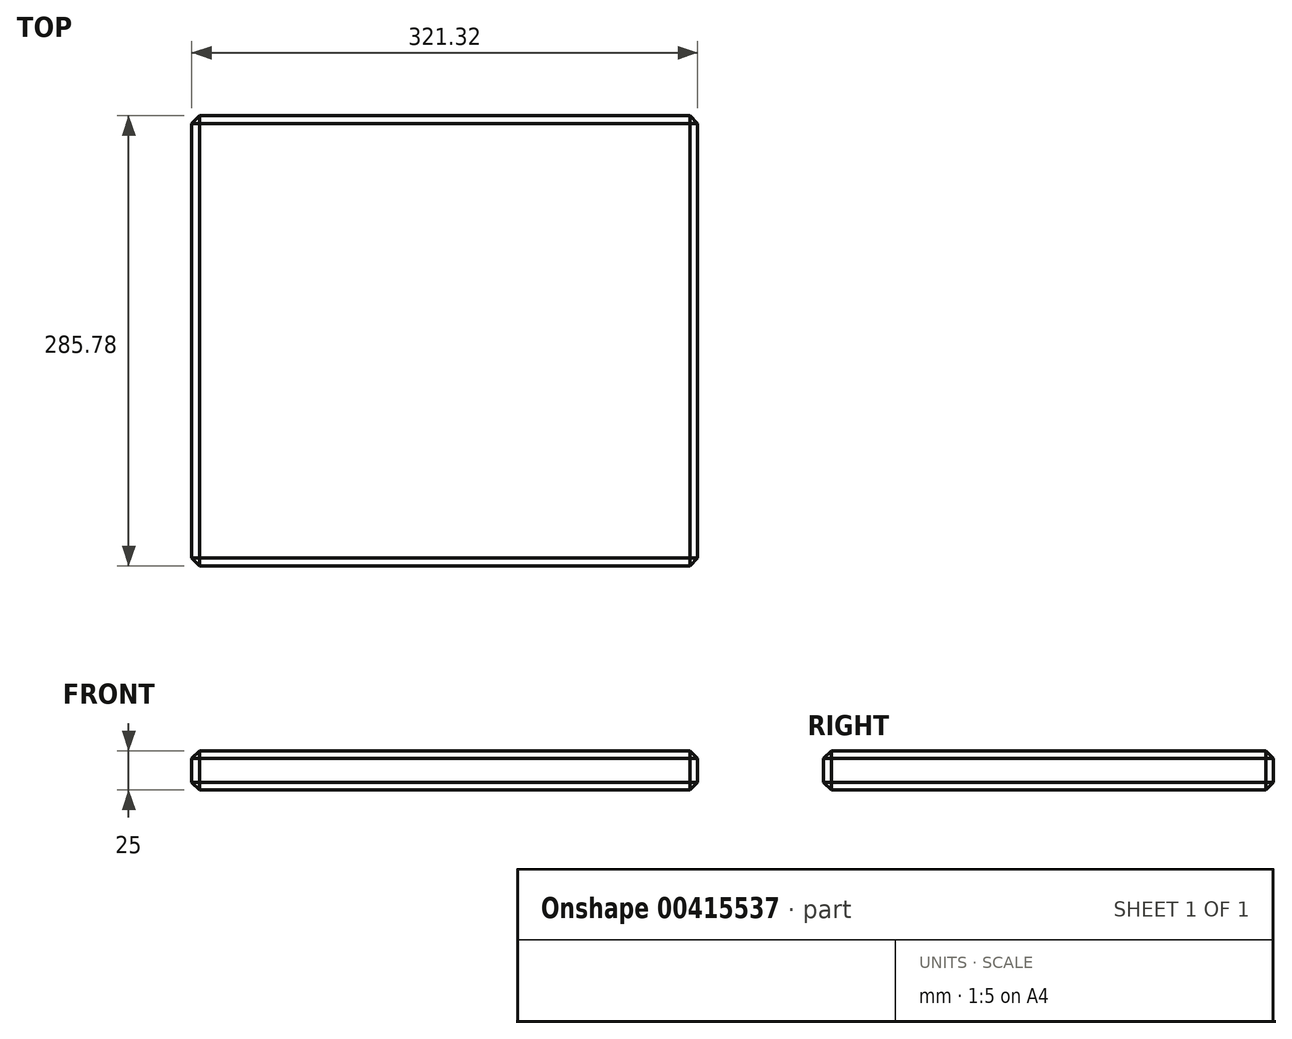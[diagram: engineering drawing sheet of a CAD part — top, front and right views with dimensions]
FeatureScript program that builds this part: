
annotation { "Feature Type Name" : "Feature", "Feature Type Description" : "" }
export const myFeature = defineFeature(function(context is Context, id is Id, definition is map)
    precondition{}
    {
        {
            var Q0;
            Q0=qCreatedBy(makeId("Top.planeOp"),FACE);
            var sketch = newSketch(context, id + "F0", { "sketchPlane" : qUnion([Q0])});
            skLineSegment(sketch, "E0.bottom", {"start": v(160.66, 142.89) * mm, "end": v(-160.66, 142.89) * mm});
            skLineSegment(sketch, "E0.top", {"start": v(160.66, -142.89) * mm, "end": v(-160.66, -142.89) * mm});
            skLineSegment(sketch, "E0.left", {"start": v(160.66, 142.89) * mm, "end": v(160.66, -142.89) * mm});
            skLineSegment(sketch, "E0.right", {"start": v(-160.66, 142.89) * mm, "end": v(-160.66, -142.89) * mm});
            skPoint(sketch, "E0.middle", {"position": v(0, 0) * mm});
            skSolve(sketch);
        }
        {
            var Q0;
            Q0=makeQuery(id+"F0.imprint","IMPRINT",FACE,{"disambiguationData":[TD([[makeQuery(id+"F0.imprint","IMPRINT",EDGE,{"derivedFrom":sQuery(id+"F0.wireOp",EDGE,"E0.bottom")}),1.0]])]});
            extrude(context, id + "F1", {"entities" : qUnion([Q0]), "depth" : 25 * mm});
        }
        {
            var Q0;
            Q0=makeQuery(id+"F1.opExtrude","SWEPT_EDGE",EDGE,{"disambiguationData":[OSD([sQuery(id+"F0.wireOp",EDGE,"E0.bottom"),sQuery(id+"F0.wireOp",EDGE,"E0.left")])]});
            var Q1;
            Q1=makeQuery(id+"F1.opExtrude","SWEPT_EDGE",EDGE,{"disambiguationData":[OSD([sQuery(id+"F0.wireOp",EDGE,"E0.top"),sQuery(id+"F0.wireOp",EDGE,"E0.left")])]});
            var Q2;
            Q2=makeQuery(id+"F1.opExtrude","CAP_EDGE",EDGE,{"disambiguationData":[OSD([sQuery(id+"F0.wireOp",EDGE,"E0.left")])],"isStart":true});
            var Q3;
            Q3=makeQuery(id+"F1.opExtrude","CAP_EDGE",EDGE,{"disambiguationData":[OSD([sQuery(id+"F0.wireOp",EDGE,"E0.top")])],"isStart":true});
            var Q4;
            Q4=makeQuery(id+"F1.opExtrude","SWEPT_FACE",FACE,{"disambiguationData":[OSD([sQuery(id+"F0.wireOp",EDGE,"E0.bottom")])]});
            var Q5;
            Q5=makeQuery(id+"F1.opExtrude","SWEPT_FACE",FACE,{"disambiguationData":[OSD([sQuery(id+"F0.wireOp",EDGE,"E0.left")])]});
            var Q6;
            Q6=makeQuery(id+"F1.opExtrude","CAP_FACE",FACE,{"disambiguationData":[OSD([sQuery(id+"F0.wireOp",EDGE,"E0.bottom"),sQuery(id+"F0.wireOp",EDGE,"E0.top"),sQuery(id+"F0.wireOp",EDGE,"E0.left"),sQuery(id+"F0.wireOp",EDGE,"E0.right")])],"isStart":false});
            var Q7;
            Q7=makeQuery(id+"F1.opExtrude","SWEPT_FACE",FACE,{"disambiguationData":[OSD([sQuery(id+"F0.wireOp",EDGE,"E0.right")])]});
            chamfer(context, id + "F2", {"entities" : qUnion([Q0, Q1, Q2, Q3, Q4, Q5, Q6, Q7]), "width" : 5 * mm, "tangentPropagation" : true});
        }
    });
